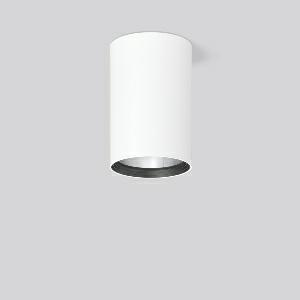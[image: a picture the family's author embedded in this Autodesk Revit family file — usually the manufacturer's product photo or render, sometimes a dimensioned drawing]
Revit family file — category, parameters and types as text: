
# Revit family: heledon_maxi_a_931238_002_43b1
name_source: partatom
category: Lighting Fixtures
units: mm (PartAtom-declared; Revit-internal decimal feet)

## family parameters
Cut with Voids When Loaded = No
Host = Face
Light Source = No
Part Type = Normal
Room Calculation Point = No
Round Connector Dimension = Use Diameter
Shared = No

## types (1)
- HELEDON maxi A (1 x LED Modul 920 meat+, 2250 lm, 2000)
    Apparent Load = 33 VA
    Approval mark = CE
    CIE Flux Codes = 100 100 100 100 100
    Color Rendering = 90
    Color Temperature = 2000
    Default Elevation = 1800 mm
    Description = Series: HELEDON maxi
Cylindrical surface-mounted downlight. Housing: die-cast aluminium, powder-coated. Internal ceiling frame polycarbonate with bayonet mounting. Black plastic ring and recessed LED to prevent glare from the side. Optical assembly with reflector made of MIRO-Silver with 98% total light reflection for outstanding efficiency - can be changed without tools. Special LED for illumination of meat included. Suitable for Ceiling mounting. Easy installation with a separate ceiling frame with bayonet mounting and plug connection. Driver integrated. Connected via plug-in connector. High quality converter without flickering and stroboscopic effect. The following accessories can be mounted without use of tools: interchangeable lenses, decorative glasses, honeycomb louvre, clear and frosted diffusers, white interchangeable plastic ring. 
Colour: traffic white, matt (RAL 9016)
Diameter: 123 mm
Height: 183 mm
Lamp: LED
Socket: without socket
Colour temperature: meat +
System power: 33 W
Rated luminous flux: 2250 lm
Luminous efficiency: 68 lm/W
Control gear: Regulated power supply
Protection class: I
Type of protection: IP 20
    Height = 183 mm
    Lamp = 1 x LED Modul 920 meat+
    Lamp Light Flux = 2250 lm
    Lamp count = 1
    Length = 123 mm
    Lifetime = 50000 h
    Luminous efficacy = 68 lm/W
    Manufacturer = RZB
    ModVariant = No
    Model = 931238.002
    Mounting Place = Ceiling
    Mounting Type = Surface mounted
    Number of Poles = 1
    OnlyDefault = Yes
    Power Factor = 1
    Product Name = HELEDON maxi A
    Product group = Surface mounted downlights
    ProductGroupID = 302
    Protection Class = Protection class I
    Protection Degree = IP 20
    RLX_Detail_Level = 1
    RLX_Emergency_Light_Flux = 0 lm
    RLX_Emergency_Type = 0
    RLX_Emergency_Type_DB = No
    RlxData = <blob elided: 98733 chars, md5=2180a1b7>
    Socket = socket
    Standby Power = 0 W
    System Light Flux = 2250 lm
    System Power = 33 W
    Type Comments = Product without accessories
    Type Image = 931192.002.jpg
    URL = http://relux.com
    VarID = ---
    Voltage = 230 V
    Voltage Range = 220-240 V
    Weight = 0.00 kg
    Width = 0 mm  [stored 0 ft]

note: [stored X ft] marks values corroborated as IEEE doubles in the binary element streams (Revit-internal decimal feet)

## geometry (parser evidence)
native form markers: Blend x4, Sweep x9
no freeform markers — native parametric forms only
